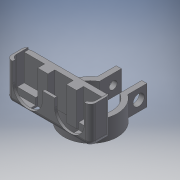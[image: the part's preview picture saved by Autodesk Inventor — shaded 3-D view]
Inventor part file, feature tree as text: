
AUTODESK INVENTOR PART (.ipt)
format: ipt  version: 2018 (Build 220112000, 112)  size: 285,184 bytes
history: native  units: in
note: dims shown in document units (in); Inventor stores cm internally (conversion verified against a paired STEP export)
features: extrude x8, sketch x8, reference x3, other x2, fillet x1, projected_geometry x1
ambient origin geometry x8: Origin, YZ Plane, XZ Plane, XY Plane, X Axis, Y Axis, Z Axis, Center Point
bodies: Solid1 (feature_tree)
feature tree (23):
  extrude  "Extrusion1"  Depth=0.125in
  extrude  "Extrusion2"  Depth=0.125in
  extrude  "Extrusion3"  Depth=0.125in
  extrude  "Extrusion4"  Depth=0.25in
  extrude  "Extrusion5"  Depth=0.194in
  extrude  "Extrusion7"  Depth=0.04in
  extrude  "Extrusion8"  Depth=0.8125in TaperAngle=0.0deg
  extrude  "Extrusion9"  Depth=0.125in
  fillet  "Fillet1"  Radius=0.05in
  sketch  "Sketch1"  dims[d0=1.05in d1=0.125in]
  sketch  "Sketch2"  dims[d2=0.125in d3=0.375in]
  sketch  "Sketch3"  dims[d4=1.0in d5=0.125in]
  sketch  "Sketch4"  dims[d6=0.5in d7=0.0in d8=0.25in]
  sketch  "Sketch5"  dims[d9=0.2in d10=0.194in]
  sketch  "Sketch7"  dims[d11=1.0in d12=0.0in d13=0.04in]
  projected_geometry  "Projected Loop3"
  sketch  "Sketch8"  dims[d14=1.0in d15=0.0in d18=0.8125in d19=0.0in]
  sketch  "Sketch9"  dims[d20=1.95in d21=0.975in d22=0.05in d23=0.05in d24=0.05in d25=0.05in d26=0.445in d27=0.0in d28=0.9125in d29=0.5in d30=0.05in d31=0.05in d35=0.17in d36=0.0in d37=0.25in d38=0.25in d39=0.5in d40=0.5in d41=0.17in d42=0.0in d43=0.05in d44=0.05in d45=0.0625in d46=0.0in d47=0.05in d48=0.125in]
  reference  "Reference1"
  reference  "Reference2"
  reference  "Reference3"
  other  "Assembly1"
  other  "Ultrasonic_sensor:1"
